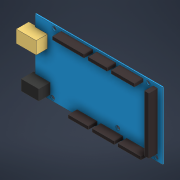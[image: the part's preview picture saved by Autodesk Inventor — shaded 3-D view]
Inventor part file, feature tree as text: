
AUTODESK INVENTOR PART (.ipt)
format: ipt  version: 2021 (Build 250183000, 183)  size: 218,624 bytes
history: native  units: mm
features: extrude x5, sketch x1
ambient origin geometry x8: Origin, YZ Plane, XZ Plane, XY Plane, X Axis, Y Axis, Z Axis, Center Point
bodies: Volumenkörper1 (feature_tree)
feature tree (6):
  sketch  "Skizze1"  dims[d0=101.6mm d1=53.34mm d2=3.2mm d3=15.24mm d4=3.2mm d5=13.97mm d6=2.54mm d7=48.26mm d8=3.2mm d9=90.17mm d10=3.2mm d11=96.52mm d12=3.2mm d13=66.04mm d14=7.62mm d15=25.0mm d16=4.0mm d17=15.0mm d18=2.5mm d19=18.5mm d20=3.5mm d21=45.0mm d22=4.0mm d23=2.5mm d24=4.0mm d25=9.0mm d26=10.0mm d27=16.0mm d28=6.0mm d29=8.5mm d30=3.5mm d31=14.0mm d32=2.0mm d33=1.0mm d34=0.0mm d35=8.0mm d36=0.0mm d37=8.0mm d38=0.0mm d41=10.0mm d42=0.0mm d43=10.0mm d44=0.0mm d39=0.5mm d40=0.872665mm]
  extrude  "Extrusion1"  Depth=53.34mm
  extrude  "Extrusion2"  Depth=0.5mm
  extrude  "Extrusion3"  Depth=0.5mm
  extrude  "Extrusion5"  Depth=0.5mm
  extrude  "Extrusion6"  Depth=0.5mm
